# Revit family: Storage-Vessel_AO_Smith-ST-300_B_E
name_source: partatom
category: Mechanical Equipment
revit_build: Autodesk Revit 2016 (Build: 20170117_1200(x64)
units: mm (PartAtom-declared; Revit-internal decimal feet)

## family parameters
Always vertical = Yes
Cut with Voids When Loaded = No
OmniClass Number = 23.75.00.00
OmniClass Title = Climate Control (HVAC)
Part Type = Normal
Room Calculation Point = No
Round Connector Dimension = Use Radius
Shared = No
Work Plane-Based = No

## types (1)
- Storage-Vessel_AO_Smith-ST-300_B_E
    1er Entretien (check-up) = 3 mois après l'installation
    2ème Entretien (Entretien Général) = 12 mois après l'installation
    Assembly Code = D3010
    BIM Content Developer = CAD & Company
    BIM Content Developer URL = http:/www.cadcompany.nl
    Capacité - Cuve = 308 m³
    Charge Maximale au Sol = 399.00 kg
    Description = Ballon de Stockage
    Destination / Pays = Belgique
    Diamètre (avec Isolation) = 750 mm  [stored 2.46063 ft]
    Diamètre (sans Isolation) = 550 mm  [stored 1.80446 ft]
    Epaisseur d'Isolation = 100 mm  [stored 0.328084 ft]
    Fabricant No. = E 7110
    Garantie Pièces = 12 mois
    Garantie sur la Cuve = 36 mois
    Guide de Produit = https://www.aosmithinternational.com
    Hauteur (avec Isolation) = 1650 mm  [stored 5.41339 ft]
    Hauteur (sans Isolation) = 1545 mm  [stored 5.0689 ft]
    Hauteur d'Emballage = 1770 mm
    Hauteur de l'Alimentation en eau Froide = 110 mm
    Hauteur de la Sortie d'eau Chaude = 1460 mm  [stored 4.79003 ft]
    Largeur = 0 mm  [stored 0 ft]
    Largeur d'Emballage = 800 mm
    Manufacturer = A.O. Smith Water Products Company b.v.
    Max. Température de l'eau - Réservoir = 95 °C
    Model = ST 300 B E
    Nombre de modèle du produit (EAN) = 8717449181703
    Poids de Transport = 107.00 kg
    Poids à vide = 99.00 kg
    Pression de Service Maximale - Réservoir = 1000000.0 Pa
    Profondeur = 0 mm  [stored 0 ft]
    Profondeur d'Emballage = 800 mm
    Raccord d'Alimentation en Eau Froide = 1"
    Raccord de Sortie d'Eau Chaude = 1"
    Raccord de la Soupape de Vidange = 1"
    Spécifications du Produit = https://www.aosmithinternational.com
    Type d'Emballage = Plastique et Bois
    URL = https://www.aosmithinternational.com
    Workspace Diameter = 1750 mm  [stored 5.74147 ft]
    Workspace Height = 2650 mm  [stored 8.69423 ft]
    espace de travail = 860 mm
    l'Intervalle d'Entretien = 12 mois

note: [stored X ft] marks values corroborated as IEEE doubles in the binary element streams (Revit-internal decimal feet)

## geometry (parser evidence)
native form markers: Blend x4, Sweep x19
no freeform markers — native parametric forms only
